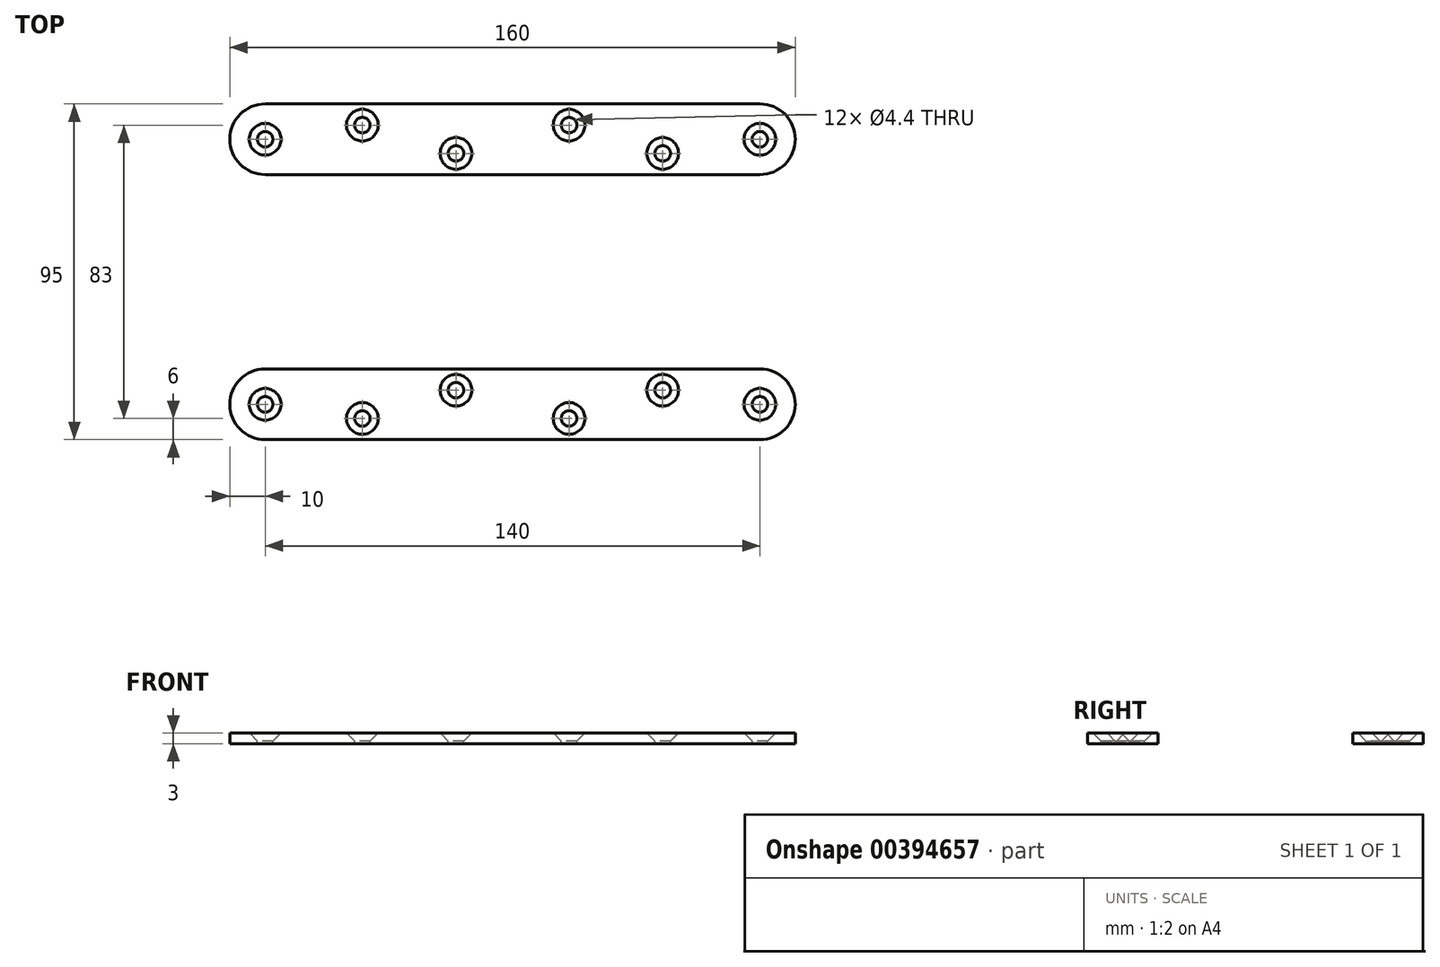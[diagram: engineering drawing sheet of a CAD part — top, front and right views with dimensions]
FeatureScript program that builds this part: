
annotation { "Feature Type Name" : "Feature", "Feature Type Description" : "" }
export const myFeature = defineFeature(function(context is Context, id is Id, definition is map)
    precondition{}
    {
        {
            var Q0;
            Q0=qCreatedBy(makeId("Top.planeOp"),FACE);
            var sketch = newSketch(context, id + "F0", { "sketchPlane" : qUnion([Q0])});
            skLineSegment(sketch, "E0.bottom", {"start": v(144.6, 72.5) * mm, "end": v(-144.6, 72.5) * mm});
            skLineSegment(sketch, "E0.top", {"start": v(144.6, -72.5) * mm, "end": v(-144.6, -72.5) * mm});
            skLineSegment(sketch, "E0.left", {"start": v(144.6, 72.5) * mm, "end": v(144.6, -72.5) * mm});
            skLineSegment(sketch, "E0.right", {"start": v(-144.6, 72.5) * mm, "end": v(-144.6, -72.5) * mm});
            skPoint(sketch, "E0.middle", {"position": v(0, 0) * mm});
            skLineSegment(sketch, "E1.bottom", {"start": v(70, 47.5) * mm, "end": v(-70, 47.5) * mm});
            skLineSegment(sketch, "E1.top", {"start": v(70, 27.5) * mm, "end": v(-70, 27.5) * mm});
            skPoint(sketch, "E1.middle", {"position": v(0, 37.5) * mm});
            skLineSegment(sketch, "E2", {"start": v(-16, 99.64) * mm, "end": v(-16, 7.8) * mm, "construction": true});
            skLineSegment(sketch, "E3", {"start": v(-42.5, 91.74) * mm, "end": v(-42.5, 3.93) * mm, "construction": true});
            skLineSegment(sketch, "E4", {"start": v(-114.5, 41.5) * mm, "end": v(126.8, 41.5) * mm, "construction": true});
            skLineSegment(sketch, "E5", {"start": v(-114.5, 33.5) * mm, "end": v(127.65, 33.5) * mm, "construction": true});
            skLineSegment(sketch, "E6", {"start": v(-80, 37.5) * mm, "end": v(80, 37.5) * mm, "construction": true});
            skPoint(sketch, "E7", {"position": v(-70, 37.5) * mm});
            skPoint(sketch, "E8", {"position": v(-42.5, 41.5) * mm});
            skPoint(sketch, "E9", {"position": v(-16, 33.5) * mm});
            skPoint(sketch, "E10", {"position": v(-16, 41.5) * mm});
            skPoint(sketch, "E11", {"position": v(-42.5, 33.5) * mm});
            skPoint(sketch, "E12.MirrorP", {"position": v(70, 37.5) * mm});
            skPoint(sketch, "E13.MirrorP", {"position": v(42.5, 41.5) * mm});
            skPoint(sketch, "E14.MirrorP", {"position": v(42.5, 33.5) * mm});
            skPoint(sketch, "E15.MirrorP", {"position": v(16, 41.5) * mm});
            skPoint(sketch, "E16.MirrorP", {"position": v(16, 33.5) * mm});
            skArc(sketch, "E17", {"start": v(70, 27.5) * mm, "mid": v(80, 37.5) * mm, "end": v(70, 47.5) * mm});
            skArc(sketch, "E18.trimOffspring", {"start": v(-70, 47.5) * mm, "mid": v(-80, 37.5) * mm, "end": v(-70, 27.5) * mm});
            skPoint(sketch, "E19.orphan", {"position": v(80, 47.5) * mm});
            skPoint(sketch, "E20.orphan", {"position": v(80, 27.5) * mm});
            skPoint(sketch, "E21.orphan", {"position": v(-80, 47.5) * mm});
            skPoint(sketch, "E22.orphan", {"position": v(-80, 27.5) * mm});
            skLineSegment(sketch, "E23", {"start": v(0, 0) * mm, "end": v(200.83, 0) * mm, "construction": true});
            skLineSegment(sketch, "E24", {"start": v(-157.1, 29) * mm, "end": v(199.6, 29) * mm, "construction": true});
            skArc(sketch, "E25.MirrorCS", {"start": v(70, 47.5) * mm, "mid": v(80, 37.5) * mm, "end": v(70, 27.5) * mm});
            skArc(sketch, "E26.MirrorCS", {"start": v(-70, 27.5) * mm, "mid": v(-80, 37.5) * mm, "end": v(-70, 47.5) * mm});
            skSolve(sketch);
        }
        {
            var Q0;
            Q0=makeQuery(id+"F0.imprint","IMPRINT",FACE,{"disambiguationData":[TD([[makeQuery(id+"F0.imprint","IMPRINT",EDGE,{"derivedFrom":sQuery(id+"F0.wireOp",EDGE,"E1.bottom")}),1.0]])]});
            var Q1;
            Q1=makeQuery(id+"F0.imprint","IMPRINT",FACE,{"disambiguationData":[TD([[makeQuery(id+"F0.imprint","IMPRINT",EDGE,{"derivedFrom":sQuery(id+"F0.wireOp",EDGE,"5698996c-6620-41f3-a2bd-e44eefb372a221.MirrorCS")}),-1.0]])]});
            extrude(context, id + "F1", {"entities" : qUnion([Q0, Q1]), "oppositeDirection" : true, "depth" : 3 * mm, "offsetDistance" : 25 * mm});
        }
        {
            var Q0;
            Q0=sQuery(id+"F0.wireOp",VERTEX,"E7");
            var Q1;
            Q1=sQuery(id+"F0.wireOp",VERTEX,"E8");
            var Q2;
            Q2=sQuery(id+"F0.wireOp",VERTEX,"E9");
            var Q3;
            Q3=sQuery(id+"F0.wireOp",VERTEX,"E15.MirrorP");
            var Q4;
            Q4=sQuery(id+"F0.wireOp",VERTEX,"E14.MirrorP");
            var Q5;
            Q5=sQuery(id+"F0.wireOp",VERTEX,"E12.MirrorP");
            var Q6;
            Q6=makeQuery(id+"F1.opExtrude","SWEPT_BODY",BODY,{"disambiguationData":[OSD([sQuery(id+"F0.wireOp",EDGE,"E1.bottom"),sQuery(id+"F0.wireOp",EDGE,"E1.top"),sQuery(id+"F0.wireOp",EDGE,"E17"),sQuery(id+"F0.wireOp",EDGE,"E18.trimOffspring")])]});
            var Q7;
            Q7=makeQuery(id+"F1.opExtrude","SWEPT_BODY",BODY,{"disambiguationData":[OSD([sQuery(id+"F0.wireOp",EDGE,"E1.bottom"),sQuery(id+"F0.wireOp",EDGE,"E25.MirrorCS"),sQuery(id+"F0.wireOp",EDGE,"E26.MirrorCS"),sQuery(id+"F0.wireOp",EDGE,"E1.top")])]});
            hole(context, id + "F2", {"style" : HoleStyle.C_SINK, "endStyle" : HoleEndStyle.THROUGH, "standardTappedOrClearance" : lookupTablePath({ "standard" : "ISO", "fit" : "Normal", "size" : "M4", "type" : "Clearance" }), "standardBlindInLast" : lookupTablePath({ "fit" : "Standard", "standard" : "ISO", "size" : "M4", "type" : "Clearance" }), "holeDiameter" : 4.4 * mm, "cSinkDiameter" : 8.96 * mm, "cSinkAngle" : 90 * degree, "majorDiameter" : 4 * mm, "tappedDepth" : 10.75 * mm, "tapClearance" : 3, "startFromSketch" : true, "locations" : qUnion([Q0, Q1, Q2, Q3, Q4, Q5]), "scope" : qUnion([Q6, Q7])});
        }
        {
            var Q0;
            Q0=makeQuery(id+"F1.opExtrude","SWEPT_BODY",BODY,{"disambiguationData":[OSD([sQuery(id+"F0.wireOp",EDGE,"E1.bottom"),sQuery(id+"F0.wireOp",EDGE,"E25.MirrorCS"),sQuery(id+"F0.wireOp",EDGE,"E26.MirrorCS"),sQuery(id+"F0.wireOp",EDGE,"E1.top")])]});
            var Q1;
            Q1=qCreatedBy(makeId("Front.planeOp"),FACE);
            mirror(context, id + "F3", {"entities" : qUnion([Q0]), "mirrorPlane" : qUnion([Q1])});
        }
    });
